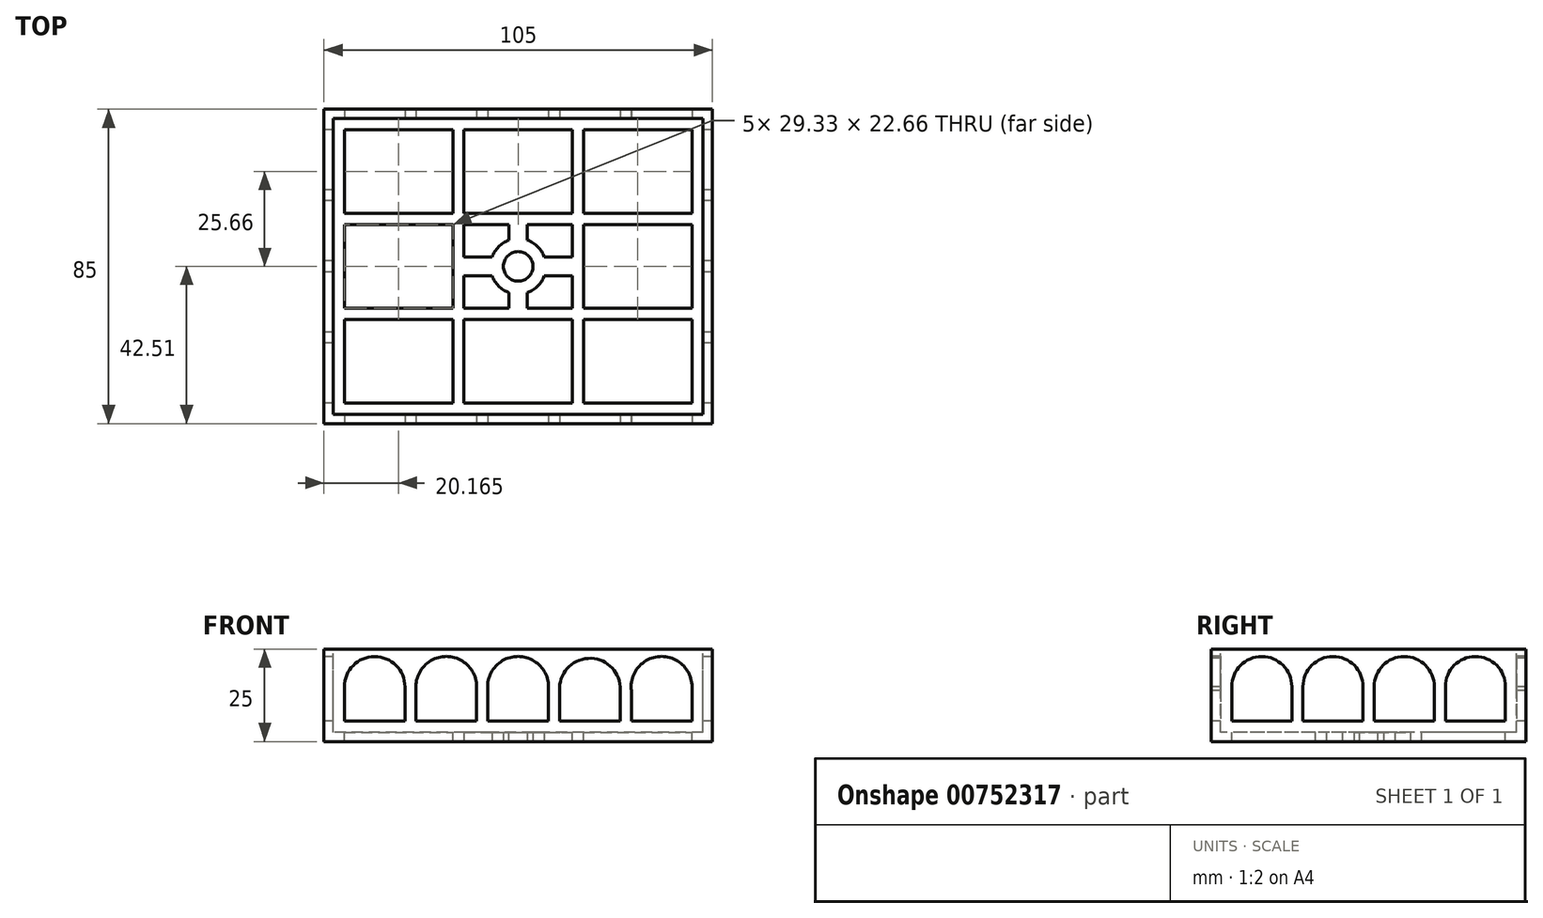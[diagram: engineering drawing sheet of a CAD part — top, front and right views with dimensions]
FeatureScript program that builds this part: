
annotation { "Feature Type Name" : "Feature", "Feature Type Description" : "" }
export const myFeature = defineFeature(function(context is Context, id is Id, definition is map)
    precondition{}
    {
        {
            var Q0;
            Q0=qCreatedBy(makeId("Top.planeOp"),FACE);
            var sketch = newSketch(context, id + "F0", { "sketchPlane" : qUnion([Q0])});
            skLineSegment(sketch, "E0.bottom", {"start": v(52.5, -42.5) * mm, "end": v(-52.5, -42.5) * mm});
            skLineSegment(sketch, "E0.top", {"start": v(52.5, 42.5) * mm, "end": v(-52.5, 42.5) * mm});
            skLineSegment(sketch, "E0.left", {"start": v(52.5, -42.5) * mm, "end": v(52.5, 42.5) * mm});
            skLineSegment(sketch, "E0.right", {"start": v(-52.5, -42.5) * mm, "end": v(-52.5, 42.5) * mm});
            skPoint(sketch, "E0.middle", {"position": v(0, 0) * mm});
            skSolve(sketch);
        }
        {
            var Q0;
            Q0=makeQuery(id+"F0.imprint","IMPRINT",FACE,{"disambiguationData":[TD([[makeQuery(id+"F0.imprint","IMPRINT",EDGE,{"derivedFrom":sQuery(id+"F0.wireOp",EDGE,"E0.bottom")}),-1.0]])]});
            extrude(context, id + "F1", {"entities" : qUnion([Q0]), "depth" : 25 * mm, "offsetDistance" : 25 * mm});
        }
        {
            var Q0;
            Q0=makeQuery(id+"F1.opExtrude","CAP_FACE",FACE,{"disambiguationData":[OSD([sQuery(id+"F0.wireOp",EDGE,"E0.bottom"),sQuery(id+"F0.wireOp",EDGE,"E0.top"),sQuery(id+"F0.wireOp",EDGE,"E0.left"),sQuery(id+"F0.wireOp",EDGE,"E0.right")])],"isStart":false});
            var sketch = newSketch(context, id + "F2", { "sketchPlane" : qUnion([Q0])});
            skLineSegment(sketch, "E1.bottom", {"start": v(50, 40) * mm, "end": v(-50, 40) * mm});
            skLineSegment(sketch, "E1.top", {"start": v(50, -40) * mm, "end": v(-50, -40) * mm});
            skLineSegment(sketch, "E1.left", {"start": v(50, 40) * mm, "end": v(50, -40) * mm});
            skLineSegment(sketch, "E1.right", {"start": v(-50, 40) * mm, "end": v(-50, -40) * mm});
            skPoint(sketch, "E1.middle", {"position": v(0, 0) * mm});
            skSolve(sketch);
        }
        {
            var Q0;
            Q0 = qSketchRegion(id + "F2", true);
            extrude(context, id + "F3", {"entities" : qUnion([Q0]), "operationType" : NewBodyOperationType.REMOVE, "oppositeDirection" : true, "depth" : 22.5 * mm, "offsetDistance" : 25 * mm});
        }
        {
            var Q0;
            Q0=makeQuery(id+"F3.boolean.opBoolean","COPY",FACE,{"derivedFrom":makeQuery(id+"F3.opExtrude","CAP_FACE",FACE,{"disambiguationData":[OSD([sQuery(id+"F2.wireOp",EDGE,"E1.bottom"),sQuery(id+"F2.wireOp",EDGE,"E1.top"),sQuery(id+"F2.wireOp",EDGE,"E1.left"),sQuery(id+"F2.wireOp",EDGE,"E1.right")])],"isStart":false})});
            var sketch = newSketch(context, id + "F4", { "sketchPlane" : qUnion([Q0])});
            skLineSegment(sketch, "E2.bottom", {"start": v(-47, 37) * mm, "end": v(-17.67, 37) * mm});
            skLineSegment(sketch, "E2.top", {"start": v(-47, 14.34) * mm, "end": v(-17.67, 14.34) * mm});
            skLineSegment(sketch, "E2.left", {"start": v(-47, 37) * mm, "end": v(-47, 14.34) * mm});
            skLineSegment(sketch, "E2.right", {"start": v(-17.67, 37) * mm, "end": v(-17.67, 14.34) * mm});
            skLineSegment(sketch, "E3.bottom", {"start": v(-14.67, 37) * mm, "end": v(14.66, 37) * mm});
            skLineSegment(sketch, "E3.top", {"start": v(-14.67, 14.34) * mm, "end": v(14.66, 14.34) * mm});
            skLineSegment(sketch, "E3.left", {"start": v(-14.67, 37) * mm, "end": v(-14.67, 14.34) * mm});
            skLineSegment(sketch, "E3.right", {"start": v(14.66, 37) * mm, "end": v(14.66, 14.34) * mm});
            skLineSegment(sketch, "E4.bottom", {"start": v(17.67, 37) * mm, "end": v(47, 37) * mm});
            skLineSegment(sketch, "E4.top", {"start": v(17.67, 14.34) * mm, "end": v(47, 14.34) * mm});
            skLineSegment(sketch, "E4.left", {"start": v(17.67, 37) * mm, "end": v(17.67, 14.34) * mm});
            skLineSegment(sketch, "E4.right", {"start": v(47, 37) * mm, "end": v(47, 14.34) * mm});
            skLineSegment(sketch, "E5.bottom", {"start": v(-47, 11.34) * mm, "end": v(-17.67, 11.34) * mm});
            skLineSegment(sketch, "E5.top", {"start": v(-47, -11.32) * mm, "end": v(-17.67, -11.32) * mm});
            skLineSegment(sketch, "E5.left", {"start": v(-47, 11.34) * mm, "end": v(-47, -11.32) * mm});
            skLineSegment(sketch, "E5.right", {"start": v(-17.67, 11.34) * mm, "end": v(-17.67, -11.32) * mm});
            skLineSegment(sketch, "E6.bottom", {"start": v(-14.67, 11.34) * mm, "end": v(14.66, 11.34) * mm});
            skLineSegment(sketch, "E6.top", {"start": v(-14.67, -11.32) * mm, "end": v(14.66, -11.32) * mm});
            skLineSegment(sketch, "E6.left", {"start": v(-14.67, 11.34) * mm, "end": v(-14.67, -11.32) * mm});
            skLineSegment(sketch, "E6.right", {"start": v(14.66, 11.34) * mm, "end": v(14.66, -11.32) * mm});
            skLineSegment(sketch, "E7.bottom", {"start": v(17.67, 11.34) * mm, "end": v(47, 11.34) * mm});
            skLineSegment(sketch, "E7.top", {"start": v(17.67, -11.32) * mm, "end": v(47, -11.32) * mm});
            skLineSegment(sketch, "E7.left", {"start": v(17.67, 11.34) * mm, "end": v(17.67, -11.32) * mm});
            skLineSegment(sketch, "E7.right", {"start": v(47, 11.34) * mm, "end": v(47, -11.32) * mm});
            skLineSegment(sketch, "E8.bottom", {"start": v(-47, -14.32) * mm, "end": v(-17.67, -14.32) * mm});
            skLineSegment(sketch, "E8.top", {"start": v(-47, -37) * mm, "end": v(-17.67, -37) * mm});
            skLineSegment(sketch, "E8.left", {"start": v(-47, -14.32) * mm, "end": v(-47, -37) * mm});
            skLineSegment(sketch, "E8.right", {"start": v(-17.67, -14.32) * mm, "end": v(-17.67, -37) * mm});
            skLineSegment(sketch, "E9.bottom", {"start": v(-14.67, -14.32) * mm, "end": v(14.66, -14.32) * mm});
            skLineSegment(sketch, "E9.top", {"start": v(-14.67, -37) * mm, "end": v(14.66, -37) * mm});
            skLineSegment(sketch, "E9.left", {"start": v(-14.67, -14.32) * mm, "end": v(-14.67, -37) * mm});
            skLineSegment(sketch, "E9.right", {"start": v(14.66, -14.32) * mm, "end": v(14.66, -37) * mm});
            skLineSegment(sketch, "E10.bottom", {"start": v(17.67, -14.32) * mm, "end": v(47, -14.32) * mm});
            skLineSegment(sketch, "E10.top", {"start": v(17.67, -37) * mm, "end": v(47, -37) * mm});
            skLineSegment(sketch, "E10.left", {"start": v(17.67, -14.32) * mm, "end": v(17.67, -37) * mm});
            skLineSegment(sketch, "E10.right", {"start": v(47, -14.32) * mm, "end": v(47, -37) * mm});
            skSolve(sketch);
        }
        {
            var Q0;
            Q0 = qSketchRegion(id + "F4", true);
            extrude(context, id + "F5", {"entities" : qUnion([Q0]), "operationType" : NewBodyOperationType.REMOVE, "oppositeDirection" : true, "depth" : 2.5 * mm, "offsetDistance" : 25 * mm});
        }
        {
            var Q0;
            Q0=makeQuery(id+"F1.opExtrude","SWEPT_FACE",FACE,{"disambiguationData":[OSD([sQuery(id+"F0.wireOp",EDGE,"E0.bottom")])]});
            var sketch = newSketch(context, id + "F6", { "sketchPlane" : qUnion([Q0])});
            skLineSegment(sketch, "E11.bottom", {"start": v(-47, 5.5) * mm, "end": v(-30.6, 5.5) * mm});
            skLineSegment(sketch, "E11.left", {"start": v(-47, 5.5) * mm, "end": v(-47, 14.8) * mm});
            skLineSegment(sketch, "E11.right", {"start": v(-30.6, 5.5) * mm, "end": v(-30.6, 14.8) * mm});
            skLineSegment(sketch, "E12.bottom", {"start": v(-27.6, 5.5) * mm, "end": v(-11.2, 5.5) * mm});
            skLineSegment(sketch, "E12.left", {"start": v(-27.6, 5.5) * mm, "end": v(-27.6, 13.8) * mm});
            skLineSegment(sketch, "E12.right", {"start": v(-11.2, 5.5) * mm, "end": v(-11.2, 14.8) * mm});
            skLineSegment(sketch, "E13.bottom", {"start": v(-8.2, 5.5) * mm, "end": v(8.2, 5.5) * mm});
            skLineSegment(sketch, "E13.left", {"start": v(-8.2, 5.5) * mm, "end": v(-8.2, 13.8) * mm});
            skLineSegment(sketch, "E13.right", {"start": v(8.2, 5.5) * mm, "end": v(8.2, 14.8) * mm});
            skLineSegment(sketch, "E14", {"start": v(-52.5, 25) * mm, "end": v(52.5, 25) * mm});
            skLineSegment(sketch, "E15.bottom", {"start": v(11.2, 5.5) * mm, "end": v(27.6, 5.5) * mm});
            skLineSegment(sketch, "E15.left", {"start": v(11.2, 5.5) * mm, "end": v(11.2, 13.8) * mm});
            skLineSegment(sketch, "E15.right", {"start": v(27.6, 5.5) * mm, "end": v(27.6, 14.8) * mm});
            skLineSegment(sketch, "E16.bottom", {"start": v(30.6, 5.5) * mm, "end": v(47, 5.5) * mm});
            skLineSegment(sketch, "E16.left", {"start": v(30.6, 5.5) * mm, "end": v(30.6, 13.8) * mm});
            skLineSegment(sketch, "E16.right", {"start": v(47, 5.5) * mm, "end": v(47, 14.8) * mm});
            skArc(sketch, "E17", {"start": v(-30.6, 14.8) * mm, "mid": v(-38.8, 23) * mm, "end": v(-47, 14.8) * mm});
            skArc(sketch, "E18", {"start": v(-11.2, 14.8) * mm, "mid": v(-19.93, 23.02) * mm, "end": v(-27.6, 13.8) * mm});
            skArc(sketch, "E19", {"start": v(8.2, 14.8) * mm, "mid": v(-0.53, 23.02) * mm, "end": v(-8.2, 13.8) * mm});
            skArc(sketch, "E20", {"start": v(27.6, 14.8) * mm, "mid": v(18.9, 22.5) * mm, "end": v(11.2, 13.8) * mm});
            skArc(sketch, "E21", {"start": v(47, 14.8) * mm, "mid": v(38.27, 23.02) * mm, "end": v(30.6, 13.8) * mm});
            skSolve(sketch);
        }
        {
            var Q0;
            Q0 = qSketchRegion(id + "F6", true);
            extrude(context, id + "F7", {"entities" : qUnion([Q0]), "operationType" : NewBodyOperationType.REMOVE, "oppositeDirection" : true, "depth" : 85 * mm, "offsetDistance" : 25 * mm});
        }
        {
            var Q0;
            Q0=makeQuery(id+"F1.opExtrude","SWEPT_FACE",FACE,{"disambiguationData":[OSD([sQuery(id+"F0.wireOp",EDGE,"E0.right")])]});
            var sketch = newSketch(context, id + "F8", { "sketchPlane" : qUnion([Q0])});
            skLineSegment(sketch, "E22.bottom", {"start": v(-37, 5.5) * mm, "end": v(-20.75, 5.5) * mm});
            skLineSegment(sketch, "E22.left", {"start": v(-37, 5.5) * mm, "end": v(-37, 14.88) * mm});
            skLineSegment(sketch, "E22.right", {"start": v(-20.75, 5.5) * mm, "end": v(-20.75, 14.88) * mm});
            skLineSegment(sketch, "E23.bottom", {"start": v(-17.75, 5.5) * mm, "end": v(-1.5, 5.5) * mm});
            skLineSegment(sketch, "E23.left", {"start": v(-17.75, 5.5) * mm, "end": v(-17.75, 14.88) * mm});
            skLineSegment(sketch, "E23.right", {"start": v(-1.5, 5.5) * mm, "end": v(-1.5, 14.88) * mm});
            skLineSegment(sketch, "E24.bottom", {"start": v(1.5, 5.5) * mm, "end": v(17.75, 5.5) * mm});
            skLineSegment(sketch, "E24.left", {"start": v(1.5, 5.5) * mm, "end": v(1.5, 14.88) * mm});
            skLineSegment(sketch, "E24.right", {"start": v(17.75, 5.5) * mm, "end": v(17.75, 14.88) * mm});
            skLineSegment(sketch, "E25.bottom", {"start": v(20.75, 5.5) * mm, "end": v(37, 5.5) * mm});
            skLineSegment(sketch, "E25.left", {"start": v(20.75, 5.5) * mm, "end": v(20.75, 14.88) * mm});
            skLineSegment(sketch, "E25.right", {"start": v(37, 5.5) * mm, "end": v(37, 14.88) * mm});
            skArc(sketch, "E26", {"start": v(-20.75, 14.88) * mm, "mid": v(-28.87, 23) * mm, "end": v(-37, 14.88) * mm});
            skArc(sketch, "E27", {"start": v(-1.5, 14.88) * mm, "mid": v(-9.62, 23) * mm, "end": v(-17.75, 14.88) * mm});
            skArc(sketch, "E28", {"start": v(17.75, 14.88) * mm, "mid": v(9.63, 23) * mm, "end": v(1.5, 14.88) * mm});
            skArc(sketch, "E29", {"start": v(37, 14.88) * mm, "mid": v(28.88, 23) * mm, "end": v(20.75, 14.88) * mm});
            skSolve(sketch);
        }
        {
            var Q0;
            Q0 = qSketchRegion(id + "F8", true);
            extrude(context, id + "F9", {"entities" : qUnion([Q0]), "operationType" : NewBodyOperationType.REMOVE, "oppositeDirection" : true, "depth" : 105 * mm, "offsetDistance" : 25 * mm});
        }
        {
            var Q0;
            Q0=qCreatedBy(makeId("Top.planeOp"),FACE);
            var sketch = newSketch(context, id + "F10", { "sketchPlane" : qUnion([Q0])});
            skLineSegment(sketch, "E30", {"start": v(-2.5, -7.07) * mm, "end": v(-2.5, -7.07) * mm});
            skLineSegment(sketch, "E31.MirrorCS", {"start": v(2.5, -7.07) * mm, "end": v(2.5, -7.07) * mm});
            skLineSegment(sketch, "E32.1.0", {"start": v(7.07, -2.5) * mm, "end": v(14.66, -2.5) * mm});
            skLineSegment(sketch, "E32.1.1", {"start": v(7.07, 2.5) * mm, "end": v(7.07, 2.5) * mm});
            skLineSegment(sketch, "E32.2.0", {"start": v(2.5, 7.07) * mm, "end": v(2.5, 11.4) * mm});
            skLineSegment(sketch, "E32.2.1", {"start": v(-2.5, 7.07) * mm, "end": v(-2.5, 11.4) * mm});
            skLineSegment(sketch, "E32.3.0", {"start": v(-7.07, 2.5) * mm, "end": v(-14.66, 2.5) * mm});
            skLineSegment(sketch, "E32.3.1", {"start": v(-7.07, -2.5) * mm, "end": v(-14.66, -2.5) * mm});
            skPoint(sketch, "E32.center", {"position": v(0, 0) * mm});
            skLineSegment(sketch, "E33", {"start": v(-2.5, -7.07) * mm, "end": v(-2.5, -11.4) * mm});
            skArc(sketch, "E34", {"start": v(-7.07, -2.5) * mm, "mid": v(-5.3, -5.3) * mm, "end": v(-2.5, -7.07) * mm});
            skArc(sketch, "E35", {"start": v(-2.5, 7.07) * mm, "mid": v(-5.3, 5.3) * mm, "end": v(-7.07, 2.5) * mm});
            skLineSegment(sketch, "E36", {"start": v(7.07, 2.5) * mm, "end": v(14.66, 2.5) * mm});
            skLineSegment(sketch, "E37", {"start": v(2.5, -7.07) * mm, "end": v(2.5, -11.4) * mm});
            skArc(sketch, "E38", {"start": v(2.5, -7.07) * mm, "mid": v(5.3, -5.3) * mm, "end": v(7.07, -2.5) * mm});
            skArc(sketch, "E39", {"start": v(7.07, 2.5) * mm, "mid": v(5.3, 5.3) * mm, "end": v(2.5, 7.07) * mm});
            skLineSegment(sketch, "E40", {"start": v(-14.66, 2.5) * mm, "end": v(-14.66, -2.5) * mm});
            skLineSegment(sketch, "E41.MirrorCS", {"start": v(14.66, 2.5) * mm, "end": v(14.66, -2.5) * mm});
            skPoint(sketch, "E42.orphan", {"position": v(-11.4, -2.5) * mm});
            skPoint(sketch, "E43.orphan", {"position": v(-11.4, 2.5) * mm});
            skPoint(sketch, "E44.orphan", {"position": v(11.4, 2.5) * mm});
            skPoint(sketch, "E45.orphan", {"position": v(11.4, -2.5) * mm});
            skLineSegment(sketch, "E46", {"start": v(-2.5, -11.4) * mm, "end": v(2.5, -11.4) * mm});
            skLineSegment(sketch, "E47", {"start": v(2.5, 11.4) * mm, "end": v(-2.5, 11.4) * mm});
            skSolve(sketch);
        }
        {
            var Q0;
            Q0 = qSketchRegion(id + "F10", true);
            extrude(context, id + "F11", {"entities" : qUnion([Q0]), "operationType" : NewBodyOperationType.ADD, "depth" : 2.5 * mm, "offsetDistance" : 25 * mm});
        }
        {
            var Q0;
            Q0=makeQuery(id+"F11.boolean.opBoolean","MERGE",FACE,{"derivedFrom":[makeQuery(id+"F1.opExtrude","CAP_FACE",FACE,{"disambiguationData":[OSD([sQuery(id+"F0.wireOp",EDGE,"E0.bottom"),sQuery(id+"F0.wireOp",EDGE,"E0.top"),sQuery(id+"F0.wireOp",EDGE,"E0.left"),sQuery(id+"F0.wireOp",EDGE,"E0.right")])],"isStart":true}),makeQuery(id+"F11.opExtrude","CAP_FACE",FACE,{"disambiguationData":[OSD([sQuery(id+"F10.wireOp",EDGE,"E32.1.0"),sQuery(id+"F10.wireOp",EDGE,"E32.2.0"),sQuery(id+"F10.wireOp",EDGE,"E32.2.1"),sQuery(id+"F10.wireOp",EDGE,"E32.3.0"),sQuery(id+"F10.wireOp",EDGE,"E32.3.1"),sQuery(id+"F10.wireOp",EDGE,"E33"),sQuery(id+"F10.wireOp",EDGE,"E34"),sQuery(id+"F10.wireOp",EDGE,"E35"),sQuery(id+"F10.wireOp",EDGE,"E36"),sQuery(id+"F10.wireOp",EDGE,"E37"),sQuery(id+"F10.wireOp",EDGE,"E38"),sQuery(id+"F10.wireOp",EDGE,"E39"),sQuery(id+"F10.wireOp",EDGE,"E40"),sQuery(id+"F10.wireOp",EDGE,"E41.MirrorCS"),sQuery(id+"F10.wireOp",EDGE,"E46"),sQuery(id+"F10.wireOp",EDGE,"E47")])],"isStart":true})]});
            var sketch = newSketch(context, id + "F12", { "sketchPlane" : qUnion([Q0])});
            skCircle(sketch, "E48", {"center": v(0, 0) * mm, "radius": 4 * mm});
            skSolve(sketch);
        }
        {
            var Q0;
            Q0 = qSketchRegion(id + "F12", true);
            extrude(context, id + "F13", {"entities" : qUnion([Q0]), "operationType" : NewBodyOperationType.REMOVE, "oppositeDirection" : true, "depth" : 2.5 * mm, "offsetDistance" : 25 * mm});
        }
    });
